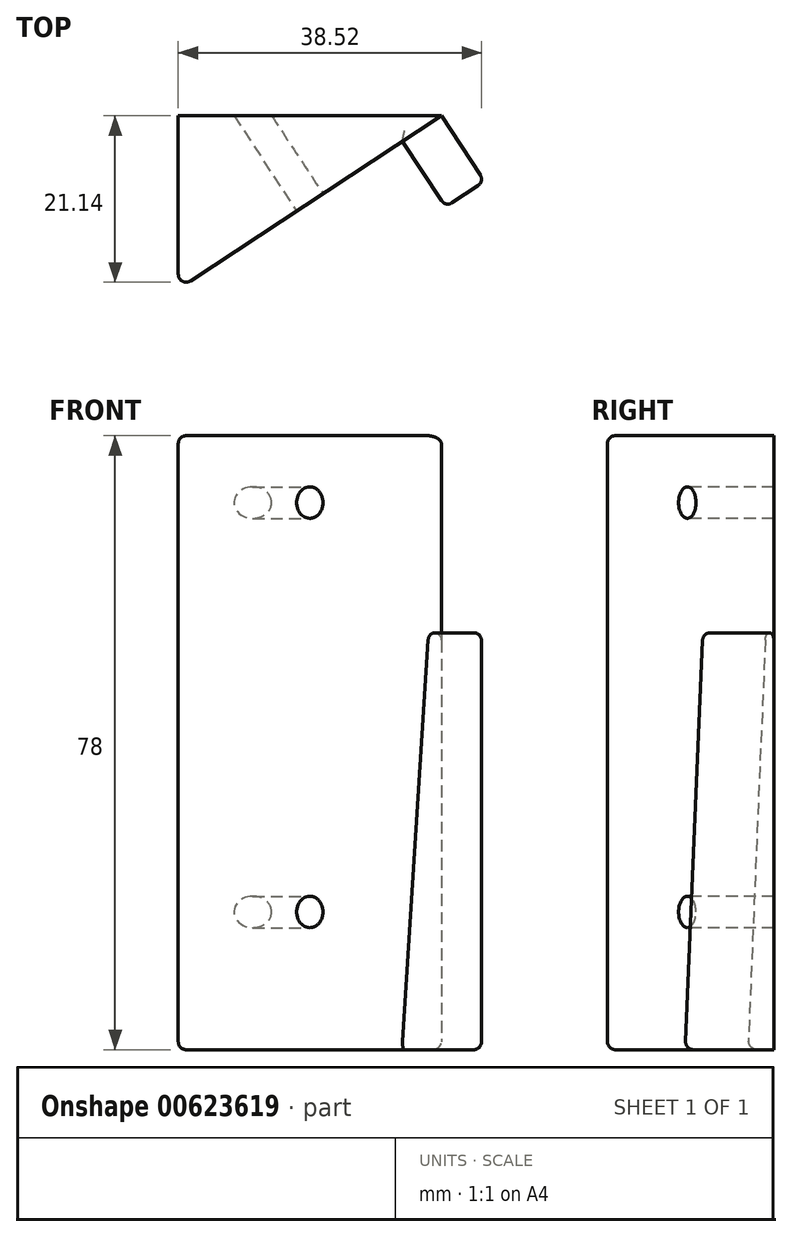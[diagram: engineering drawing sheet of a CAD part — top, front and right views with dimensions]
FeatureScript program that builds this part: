
annotation { "Feature Type Name" : "Feature", "Feature Type Description" : "" }
export const myFeature = defineFeature(function(context is Context, id is Id, definition is map)
    precondition{}
    {
        {
            var Q0;
            Q0=qCreatedBy(makeId("Top.planeOp"),FACE);
            var sketch = newSketch(context, id + "F0", { "sketchPlane" : qUnion([Q0])});
            skLineSegment(sketch, "E0", {"start": v(0, 0) * mm, "end": v(33.4, 22) * mm});
            skLineSegment(sketch, "E1", {"start": v(33.4, 22) * mm, "end": v(0, 22) * mm});
            skLineSegment(sketch, "E2", {"start": v(0, 22) * mm, "end": v(0, 0) * mm});
            skSolve(sketch);
        }
        {
            var Q0;
            Q0=makeQuery(id+"F0.imprint","IMPRINT",FACE,{"disambiguationData":[TD([[makeQuery(id+"F0.imprint","IMPRINT",EDGE,{"derivedFrom":sQuery(id+"F0.wireOp",EDGE,"E0")}),1.0]])]});
            extrude(context, id + "F1", {"entities" : qUnion([Q0]), "depth" : 78 * mm, "offsetDistance" : 25 * mm});
        }
        {
            var Q0;
            Q0=makeQuery(id+"F1.opExtrude","SWEPT_FACE",FACE,{"disambiguationData":[OSD([sQuery(id+"F0.wireOp",EDGE,"E0")])]});
            var sketch = newSketch(context, id + "F2", { "sketchPlane" : qUnion([Q0])});
            skLineSegment(sketch, "E3", {"start": v(20, 78) * mm, "end": v(20, 0) * mm, "construction": true});
            skCircle(sketch, "E4", {"center": v(20, 69.5) * mm, "radius": 2 * mm});
            skCircle(sketch, "E5", {"center": v(20, 17.5) * mm, "radius": 2 * mm});
            skLineSegment(sketch, "E6", {"start": v(40, 78) * mm, "end": v(34, 0) * mm});
            skSolve(sketch);
        }
        {
            var Q0;
            Q0=makeQuery(id+"F2.imprint","IMPRINT",FACE,{"disambiguationData":[TD([[makeQuery(id+"F2.imprint","IMPRINT",EDGE,{"derivedFrom":sQuery(id+"F2.wireOp",EDGE,"E4")}),1.0]])]});
            var Q1;
            Q1=makeQuery(id+"F2.imprint","IMPRINT",FACE,{"disambiguationData":[TD([[makeQuery(id+"F2.imprint","IMPRINT",EDGE,{"derivedFrom":sQuery(id+"F2.wireOp",EDGE,"E5")}),1.0]])]});
            var Q2;
            Q2=sQuery(id+"F2.wireOp",EDGE,"E4");
            var Q3;
            Q3=sQuery(id+"F2.wireOp",EDGE,"E5");
            extrude(context, id + "F3", {"entities" : qUnion([Q0, Q1]), "operationType" : NewBodyOperationType.REMOVE, "surfaceEntities" : qUnion([Q2, Q3]), "oppositeDirection" : true, "depth" : 25 * mm, "offsetDistance" : 25 * mm});
        }
        {
            var Q0;
            {var subQ0=sQuery(id+"F2.wireOp",EDGE,"E6");Q0=makeQuery(id+"F2.imprint","IMPRINT",FACE,{"disambiguationData":[TD([[makeQuery(id+"F2.imprint","IMPRINT",EDGE,{"derivedFrom":subQ0}),1.0]])]});}
            extrude(context, id + "F4", {"entities" : qUnion([Q0]), "operationType" : NewBodyOperationType.ADD, "depth" : 10 * mm, "offsetDistance" : 25 * mm});
        }
        {
            var Q0;
            Q0=makeQuery(id+"F4.opExtrude","SWEPT_EDGE",EDGE,{"disambiguationData":[OSD([sQuery(id+"F0.wireOp",EDGE,"E0"),sQuery(id+"F0.wireOp",EDGE,"E1"),sQuery(id+"F2.wireOp",EDGE,"E6")])]});
            var Q1;
            Q1=makeQuery(id+"F4.opExtrude","CAP_FACE",FACE,{"disambiguationData":[OSD([sQuery(id+"F0.wireOp",EDGE,"E0"),sQuery(id+"F0.wireOp",EDGE,"E1"),sQuery(id+"F2.wireOp",EDGE,"E6")])],"isStart":false});
            var Q2;
            Q2=makeQuery(id+"F4.opExtrude","SWEPT_EDGE",EDGE,{"disambiguationData":[OSD([sQuery(id+"F0.wireOp",EDGE,"E0"),sQuery(id+"F2.wireOp",EDGE,"E6")])]});
            var Q3;
            Q3=makeQuery(id+"F4.opExtrude","SWEPT_EDGE",EDGE,{"disambiguationData":[OSD([sQuery(id+"F0.wireOp",EDGE,"E0"),sQuery(id+"F0.wireOp",EDGE,"E1")])]});
            fillet(context, id + "F5", {"entities" : qUnion([Q0, Q1, Q2, Q3]), "radius" : 1 * mm, "tangentPropagation" : true, "allowEdgeOverflow" : false});
        }
        {
            var Q0;
            Q0=makeQuery(id+"F1.opExtrude","CAP_EDGE",EDGE,{"disambiguationData":[OSD([sQuery(id+"F0.wireOp",EDGE,"E0")])],"isStart":true});
            var Q1;
            Q1=makeQuery(id+"F1.opExtrude","SWEPT_EDGE",EDGE,{"disambiguationData":[OSD([sQuery(id+"F0.wireOp",EDGE,"E0"),sQuery(id+"F0.wireOp",EDGE,"E2")])]});
            var Q2;
            Q2=makeQuery(id+"F1.opExtrude","CAP_EDGE",EDGE,{"disambiguationData":[OSD([sQuery(id+"F0.wireOp",EDGE,"E0")])],"isStart":false});
            var Q3;
            Q3=makeQuery(id+"F1.opExtrude","CAP_EDGE",EDGE,{"disambiguationData":[OSD([sQuery(id+"F0.wireOp",EDGE,"E2")])],"isStart":true});
            var Q4;
            Q4=makeQuery(id+"F1.opExtrude","CAP_EDGE",EDGE,{"disambiguationData":[OSD([sQuery(id+"F0.wireOp",EDGE,"E2")])],"isStart":false});
            var Q5;
            Q5=makeQuery(id+"F3.boolean.opBoolean","COPY",EDGE,{"derivedFrom":makeQuery(id+"F3.opExtrude","CAP_EDGE",EDGE,{"disambiguationData":[OSD([sQuery(id+"F2.wireOp",EDGE,"E4")])],"isStart":true})});
            var Q6;
            Q6=makeQuery(id+"F3.boolean.opBoolean","COPY",EDGE,{"derivedFrom":makeQuery(id+"F3.opExtrude","CAP_EDGE",EDGE,{"disambiguationData":[OSD([sQuery(id+"F2.wireOp",EDGE,"E5")])],"isStart":true})});
            fillet(context, id + "F6", {"entities" : qUnion([Q0, Q1, Q2, Q3, Q4, Q5, Q6]), "radius" : 1 * mm, "tangentPropagation" : true, "allowEdgeOverflow" : false});
        }
    });
